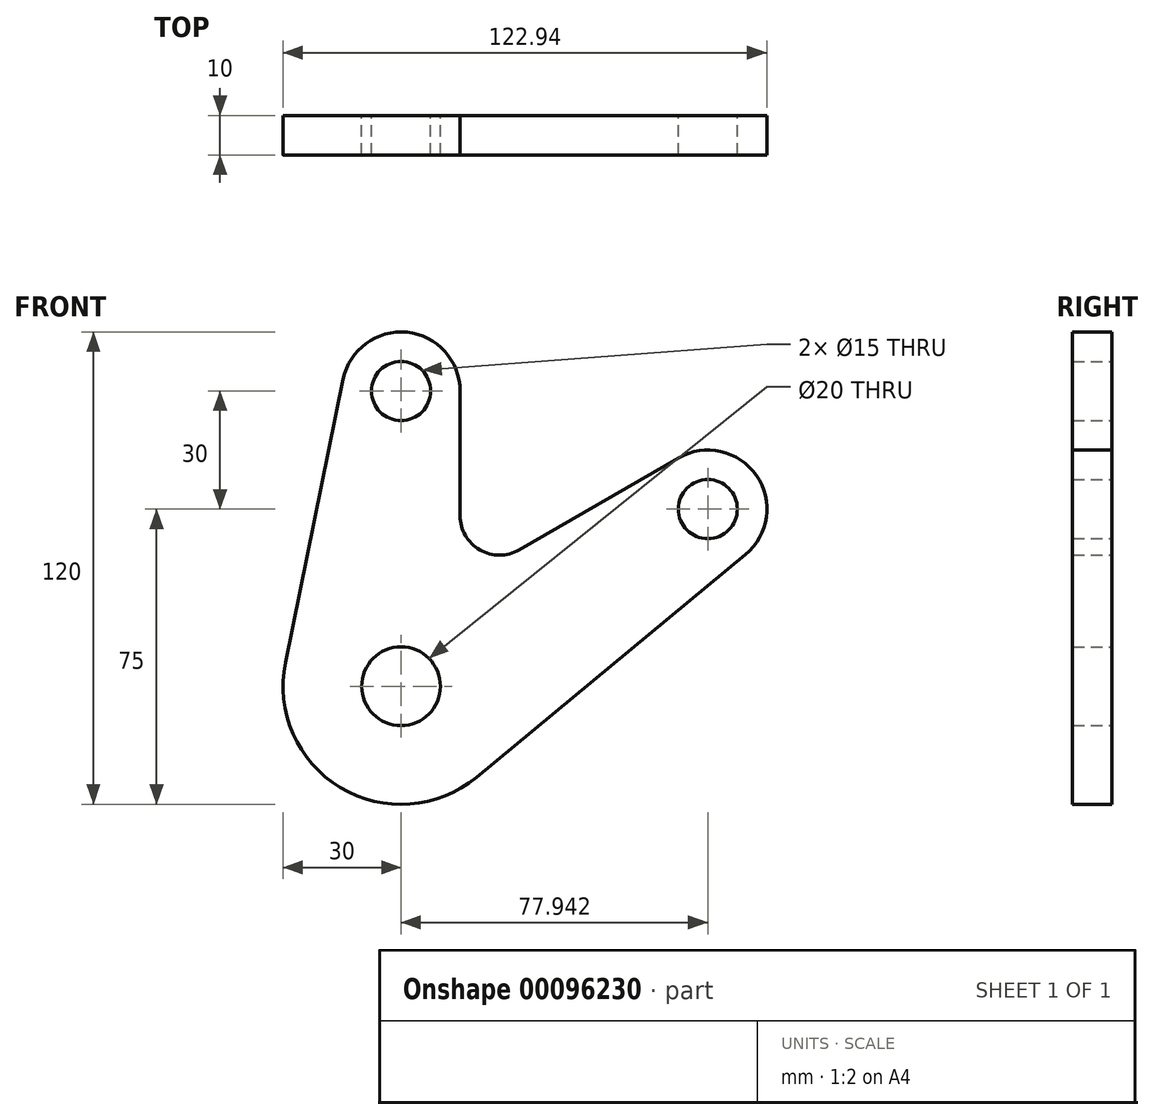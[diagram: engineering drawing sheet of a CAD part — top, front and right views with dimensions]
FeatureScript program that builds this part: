
annotation { "Feature Type Name" : "Feature", "Feature Type Description" : "" }
export const myFeature = defineFeature(function(context is Context, id is Id, definition is map)
    precondition{}
    {
        {
            var Q0;
            Q0=qCreatedBy(makeId("Front.planeOp"),FACE);
            var sketch = newSketch(context, id + "F0", { "sketchPlane" : qUnion([Q0])});
            skLineSegment(sketch, "E0", {"start": v(0, 0) * mm, "end": v(0, 75) * mm, "construction": true});
            skLineSegment(sketch, "E1", {"start": v(0, 0) * mm, "end": v(77.94, 45) * mm, "construction": true});
            skCircle(sketch, "E2", {"center": v(0, 75) * mm, "radius": 7.5 * mm});
            skCircle(sketch, "E3", {"center": v(77.94, 45) * mm, "radius": 7.5 * mm});
            skCircle(sketch, "E4", {"center": v(0, 0) * mm, "radius": 10 * mm});
            skArc(sketch, "E5", {"start": v(19.12, -23.12) * mm, "mid": v(-15.44, -25.72) * mm, "end": v(-29.4, 6) * mm});
            skArc(sketch, "E6", {"start": v(-14.7, 78) * mm, "mid": v(1.5, 89.92) * mm, "end": v(15, 75) * mm});
            skArc(sketch, "E7", {"start": v(70.44, 58) * mm, "mid": v(90.26, 53.56) * mm, "end": v(87.5, 33.44) * mm});
            skLineSegment(sketch, "E8", {"start": v(-29.4, 6) * mm, "end": v(-14.7, 78) * mm});
            skLineSegment(sketch, "E9", {"start": v(19.12, -23.12) * mm, "end": v(87.5, 33.44) * mm});
            skLineSegment(sketch, "E10", {"start": v(70.44, 58) * mm, "end": v(30, 34.64) * mm});
            skLineSegment(sketch, "E11", {"start": v(15, 43.3) * mm, "end": v(15, 75) * mm});
            skPoint(sketch, "E12.visualSharp", {"position": v(15, 25.98) * mm});
            skArc(sketch, "E12.filletArc", {"start": v(15, 43.3) * mm, "mid": v(20, 34.64) * mm, "end": v(30, 34.64) * mm});
            skSolve(sketch);
        }
        {
            var Q0;
            Q0=makeQuery(id+"F0.imprint","IMPRINT",FACE,{"disambiguationData":[TD([[makeQuery(id+"F0.imprint","IMPRINT",EDGE,{"derivedFrom":sQuery(id+"F0.wireOp",EDGE,"E2")}),-1.0]])]});
            extrude(context, id + "F1", {"entities" : qUnion([Q0]), "depth" : 10 * mm});
        }
    });
